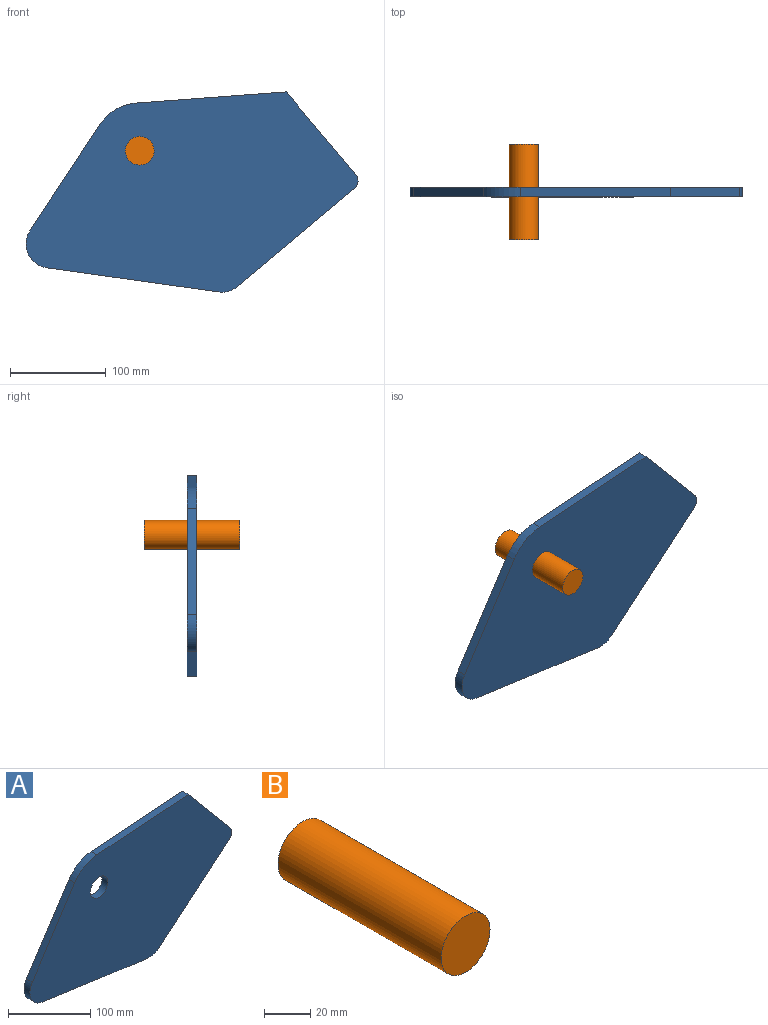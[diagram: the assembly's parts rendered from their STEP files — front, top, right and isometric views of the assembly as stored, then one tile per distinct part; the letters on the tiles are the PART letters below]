
ASSEMBLY  parts=2 mates=1
PART A: 12 faces, bbox 347.2x10x209.5 mm
  f0: cylinder r=25mm len=19.55mm, axis (0,1,0), area 209.4mm2, adj f1,f7,f8,f9
  f1: plane 122.57x102.85mm, normal (0.64,0,-0.77), area 1600mm2, adj f0,f8,f9,f10
  f2: plane 86.68x72.73mm, normal (0.77,0,0.64), area 1131.5mm2, adj f3,f8,f9,f10
  f3: plane 156.9x11.73mm, normal (-0.07,0,1), area 1573.4mm2, adj f2,f4,f8,f9
  f4: cylinder r=50mm len=38.07mm, axis (0,1,0), area 457.6mm2, adj f3,f5,f8,f9
  f5: plane 111.3x73.06mm, normal (-0.84,0,0.55), area 1331.4mm2, adj f4,f6,f8,f9
  f6: cylinder r=25mm len=38.48mm, axis (0,1,0), area 503mm2, adj f5,f7,f8,f9
  f7: plane 180x25.3mm, normal (-0.14,0,-0.99), area 1817.7mm2, adj f0,f6,f8,f9
  f8: plane 347.21x209.46mm, normal (0,-1,0), area 49399.6mm2, adj f0,f1,f2,f3,f4,f5,f6,f7
  f9: plane 347.21x209.46mm, normal (0,1,0), area 49399.6mm2, adj f0,f1,f2,f3,f4,f5,f6,f7
  f10: cylinder r=10mm len=14.09mm, axis (0,1,0), area 157.1mm2, adj f1,f2,f8,f9
  f11: cylinder r=15mm len=30mm, axis (0,-1,0), area 942.5mm2, adj f8,f9
PART B: 3 faces, bbox 30x100x30 mm
  f0: cylinder r=15mm len=100mm, axis (0,1,0), area 9424.8mm2, adj f1,f2
  f1: plane 30x30mm, normal (0,-1,0), area 706.9mm2, adj f0
  f2: plane 30x30mm, normal (0,1,0), area 706.9mm2, adj f0
PLACE A rot(axis=(0,-1,0.01),0deg) t=(86.04,0,-122.87)mm
PLACE B at identity fixed
MATE revolute B.f0 <-> A.f4  axis (0,1,0) through (0,0,0)mm
